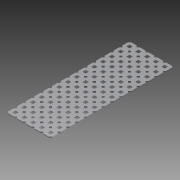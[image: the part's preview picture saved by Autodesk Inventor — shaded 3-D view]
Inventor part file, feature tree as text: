
AUTODESK INVENTOR PART (.ipt)
format: ipt  version: 2014 SP1 (Build 180222100, 222)  size: 794,624 bytes
history: native  units: in
note: dims shown in document units (in); Inventor stores cm internally (conversion verified against a paired STEP export)
features: other x1, imported_body x1, extrude x1, sketch x1
ambient origin geometry x8: Origin, YZ Plane, XZ Plane, XY Plane, X Axis, Y Axis, Z Axis, Center Point
bodies: Body1 (feature_tree)
feature tree (4):
  parser-record x1  (decoder bookkeeping rows leaked as tree rows — omitted from the tree; the rows remain in map.json)
  imported_body  "Base1"
  extrude  "Extrusion1"  Depth=1.0in TaperAngle=0.0deg
  sketch  "Sketch1"  dims[d0=0.5in d1=1.0in d2=0.0in]
